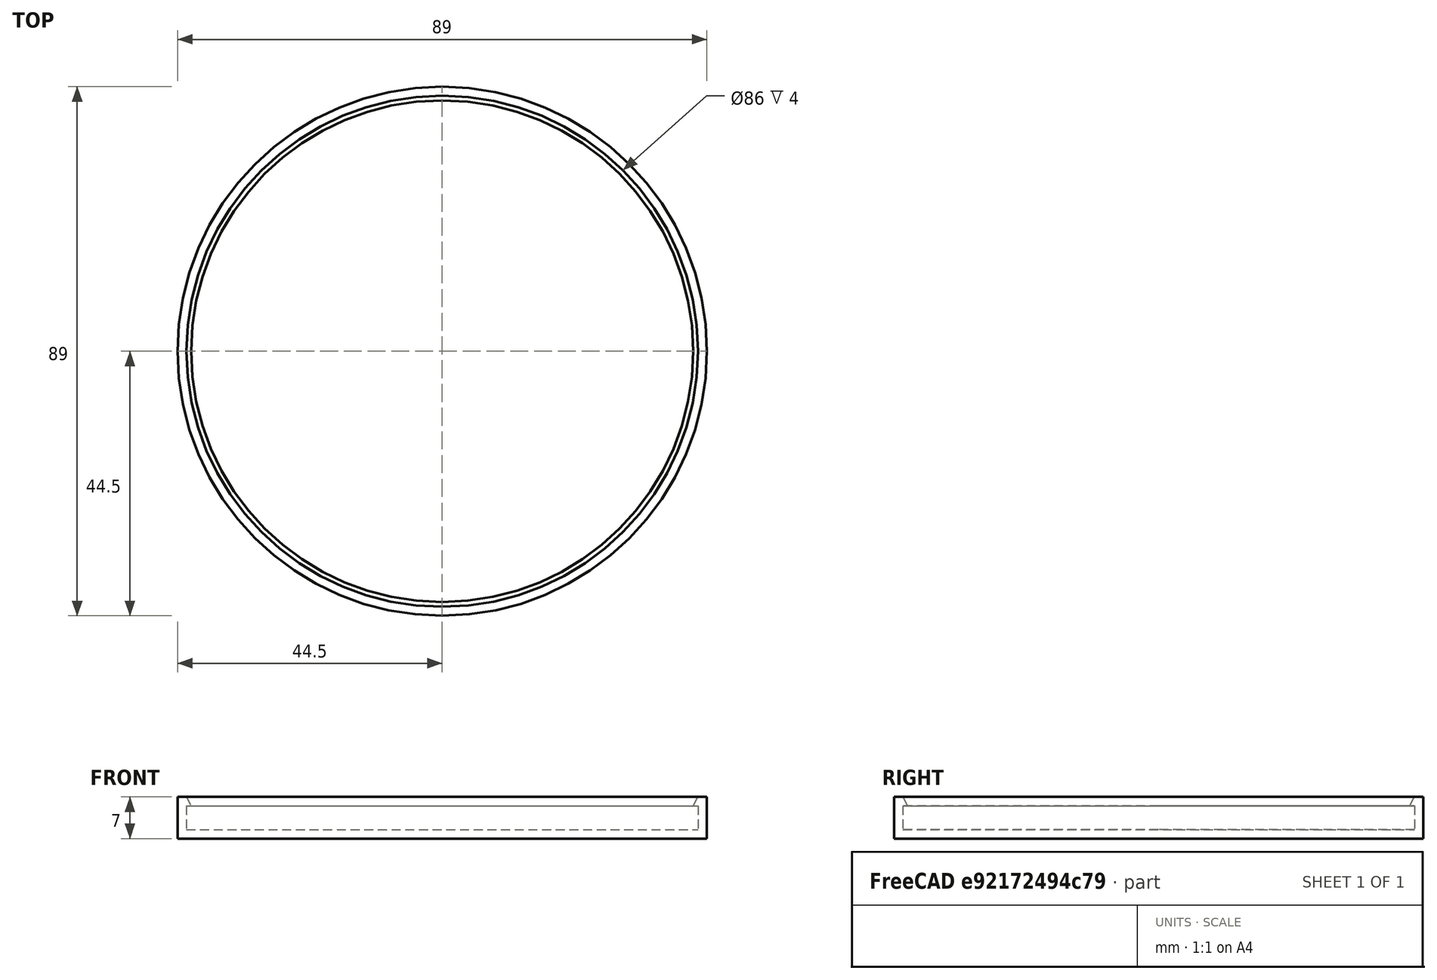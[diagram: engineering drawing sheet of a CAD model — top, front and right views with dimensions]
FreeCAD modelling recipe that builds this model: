
FCSTD DOCUMENT  (FreeCAD 0.20R29177 +426 (Git))
Label: pet_food_lid_85mm
License: Creative Commons Attribution
LicenseURL: http://creativecommons.org/licenses/by/3.0/
objects: Sketcher::SketchObject×1, PartDesign::Revolution×1, PartDesign::Body×1, Mesh::Feature×1
note: 4 computed .brp shape members not serialized (recipe doc carries the construction recipe); baked Part::Feature solids carry a one-line shape summary decoded from their .brp

FEATURE [Sketcher::SketchObject] Sketch
  FullyConstrained = true
  MapMode = 5
  Placement = pos=(0,0,0) rot=(1,0,0;1.5708rad)
  Support = -> [XZ_Plane]
  expr: Constraints[16] = 86 / 2
  expr: Constraints[19] = 84.40000000000001 / 2
  expr: Constraints[21] = .Constraints.top_thickness * 2 + .Constraints.rim_thickness
  expr: Constraints[22] = .Constraints.top_thickness
  sketch-geometry (8):
    g0: LineSegment StartX=0 StartY=0 StartZ=0 EndX=-44.5 EndY=0 EndZ=0
    g1: LineSegment StartX=-44.5 StartY=0 StartZ=0 EndX=-44.5 EndY=7 EndZ=0
    g2: LineSegment StartX=-44.5 StartY=7 StartZ=0 EndX=-43 EndY=7 EndZ=0
    g3: LineSegment StartX=-43 StartY=7 StartZ=0 EndX=-42.2 EndY=5.5 EndZ=0
    g4: LineSegment StartX=-42.2 StartY=5.5 StartZ=0 EndX=-43 EndY=5.5 EndZ=0
    g5: LineSegment StartX=-43 StartY=5.5 StartZ=0 EndX=-43 EndY=1.5 EndZ=0
    g6: LineSegment StartX=-43 StartY=1.5 StartZ=0 EndX=0 EndY=1.5 EndZ=0
    g7: LineSegment StartX=0 StartY=1.5 StartZ=0 EndX=0 EndY=0 EndZ=0
  constraints (23):
    c: Coincident(g-1,g0)
    c: PointOnObject(g0,g-1)
    c: Coincident(g0,g1)
    c: Vertical(g1)
    c: Coincident(g1,g2)
    c: Horizontal(g2)
    c: Coincident(g2,g3)
    c: Coincident(g3,g4)
    c: Horizontal(g4)
    c: Coincident(g4,g5)
    c: Vertical(g5)
    c: Coincident(g5,g6)
    c: PointOnObject(g6,g-2)
    c: Horizontal(g6)
    c: Coincident(g6,g7)
    c: Coincident(g7,g0)
    c: DistanceX(g5,g6) = 43
    c: DistanceY(g0,g6) = 1.5  'top_thickness'
    c: DistanceX(g0,g5) = 1.5
    c: DistanceX(g3,g6) = 42.2
    c: DistanceY(g5,g4) = 4  'rim_thickness'
    c: DistanceY(g0,g1) = 7
    c: DistanceX(g1,g2) = 1.5
FEATURE [PartDesign::Revolution] Revolution
  Angle = 360
  Axis = (0,-2e-16,1)
  Base = (0,0,0)
  Placement = pos=(0,0,0) rot=(1,0,0;1.5708rad)
  Profile = -> Sketch
  ReferenceAxis = -> Sketch [V_Axis]
FEATURE [PartDesign::Body] Body
  Group = -> [Sketch,Revolution]
  Origin = -> Origin
  Tip = -> Revolution
FEATURE [Mesh::Feature] Mesh  label="Revolution (Meshed)"
